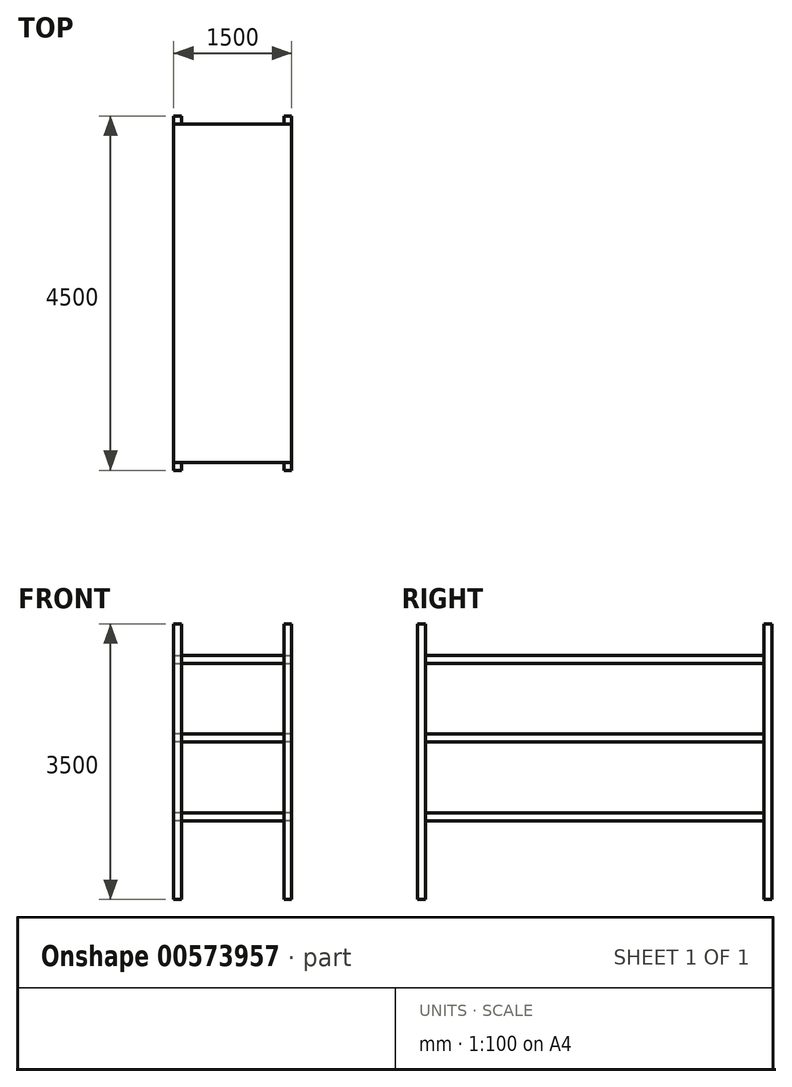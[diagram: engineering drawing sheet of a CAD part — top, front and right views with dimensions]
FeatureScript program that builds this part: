
annotation { "Feature Type Name" : "Feature", "Feature Type Description" : "" }
export const myFeature = defineFeature(function(context is Context, id is Id, definition is map)
    precondition{}
    {
        {
            var Q0;
            Q0=qCreatedBy(makeId("Top.planeOp"),FACE);
            cPlane(context, id + "F0", {"entities" : qUnion([Q0]), "cplaneType" : CPlaneType.OFFSET, "offset" : 1000 * mm, "width" : 150 * mm, "height" : 150 * mm});
        }
        {
            var Q0;
            Q0=qCreatedBy(makeId("Top.planeOp"),FACE);
            cPlane(context, id + "F1", {"entities" : qUnion([Q0]), "cplaneType" : CPlaneType.OFFSET, "offset" : 2000 * mm, "width" : 150 * mm, "height" : 150 * mm});
        }
        {
            var Q0;
            Q0=qCreatedBy(makeId("Top.planeOp"),FACE);
            cPlane(context, id + "F2", {"entities" : qUnion([Q0]), "cplaneType" : CPlaneType.OFFSET, "offset" : 3000 * mm, "width" : 150 * mm, "height" : 150 * mm});
        }
        {
            var Q0;
            Q0=qCreatedBy(makeId("Top.planeOp"),FACE);
            var sketch = newSketch(context, id + "F3", { "sketchPlane" : qUnion([Q0])});
            skPoint(sketch, "E0.middle", {"position": v(0, 0) * mm});
            skLineSegment(sketch, "E1.bottom", {"start": v(-750, 2250) * mm, "end": v(-650, 2250) * mm});
            skLineSegment(sketch, "E1.top", {"start": v(-750, 2150) * mm, "end": v(-650, 2150) * mm});
            skLineSegment(sketch, "E1.left", {"start": v(-750, 2250) * mm, "end": v(-750, 2150) * mm});
            skLineSegment(sketch, "E1.right", {"start": v(-650, 2250) * mm, "end": v(-650, 2150) * mm});
            skLineSegment(sketch, "E2.bottom", {"start": v(750, 2250) * mm, "end": v(650, 2250) * mm});
            skLineSegment(sketch, "E2.top", {"start": v(750, 2150) * mm, "end": v(650, 2150) * mm});
            skLineSegment(sketch, "E2.left", {"start": v(750, 2250) * mm, "end": v(750, 2150) * mm});
            skLineSegment(sketch, "E2.right", {"start": v(650, 2250) * mm, "end": v(650, 2150) * mm});
            skLineSegment(sketch, "E3.bottom", {"start": v(-750, -2250) * mm, "end": v(-650, -2250) * mm});
            skLineSegment(sketch, "E3.top", {"start": v(-750, -2150) * mm, "end": v(-650, -2150) * mm});
            skLineSegment(sketch, "E3.left", {"start": v(-750, -2250) * mm, "end": v(-750, -2150) * mm});
            skLineSegment(sketch, "E3.right", {"start": v(-650, -2250) * mm, "end": v(-650, -2150) * mm});
            skLineSegment(sketch, "E4.bottom", {"start": v(750, -2250) * mm, "end": v(650, -2250) * mm});
            skLineSegment(sketch, "E4.top", {"start": v(750, -2150) * mm, "end": v(650, -2150) * mm});
            skLineSegment(sketch, "E4.left", {"start": v(750, -2250) * mm, "end": v(750, -2150) * mm});
            skLineSegment(sketch, "E4.right", {"start": v(650, -2250) * mm, "end": v(650, -2150) * mm});
            skSolve(sketch);
        }
        {
            var Q0;
            Q0=qCreatedBy(id+"F0.planeOp",FACE);
            var sketch = newSketch(context, id + "F4", { "sketchPlane" : qUnion([Q0])});
            skLineSegment(sketch, "E5.bottom", {"start": v(750, -2150) * mm, "end": v(-750, -2150) * mm});
            skLineSegment(sketch, "E5.top", {"start": v(750, 2150) * mm, "end": v(-750, 2150) * mm});
            skLineSegment(sketch, "E5.left", {"start": v(750, -2150) * mm, "end": v(750, 2150) * mm});
            skLineSegment(sketch, "E5.right", {"start": v(-750, -2150) * mm, "end": v(-750, 2150) * mm});
            skPoint(sketch, "E5.middle", {"position": v(0, 0) * mm});
            skSolve(sketch);
        }
        {
            var Q0;
            Q0=qCreatedBy(id+"F1.planeOp",FACE);
            var sketch = newSketch(context, id + "F5", { "sketchPlane" : qUnion([Q0])});
            skLineSegment(sketch, "E6.bottom", {"start": v(750, 2150) * mm, "end": v(-750, 2150) * mm});
            skLineSegment(sketch, "E6.top", {"start": v(750, -2150) * mm, "end": v(-750, -2150) * mm});
            skLineSegment(sketch, "E6.left", {"start": v(750, 2150) * mm, "end": v(750, -2150) * mm});
            skLineSegment(sketch, "E6.right", {"start": v(-750, 2150) * mm, "end": v(-750, -2150) * mm});
            skPoint(sketch, "E6.middle", {"position": v(0, 0) * mm});
            skSolve(sketch);
        }
        {
            var Q0;
            Q0=qCreatedBy(id+"F2.planeOp",FACE);
            var sketch = newSketch(context, id + "F6", { "sketchPlane" : qUnion([Q0])});
            skLineSegment(sketch, "E7.bottom", {"start": v(-750, -2150) * mm, "end": v(750, -2150) * mm});
            skLineSegment(sketch, "E7.top", {"start": v(-750, 2150) * mm, "end": v(750, 2150) * mm});
            skLineSegment(sketch, "E7.left", {"start": v(-750, -2150) * mm, "end": v(-750, 2150) * mm});
            skLineSegment(sketch, "E7.right", {"start": v(750, -2150) * mm, "end": v(750, 2150) * mm});
            skPoint(sketch, "E7.middle", {"position": v(0, 0) * mm});
            skSolve(sketch);
        }
        {
            var Q0;
            Q0 = qSketchRegion(id + "F3", true);
            extrude(context, id + "F7", {"entities" : qUnion([Q0]), "depth" : 3500 * mm, "offsetDistance" : 25 * mm});
        }
        {
            var Q0;
            Q0 = qSketchRegion(id + "F4", true);
            var Q1;
            Q1 = qSketchRegion(id + "F5", true);
            extrude(context, id + "F8", {"entities" : qUnion([Q0, Q1]), "depth" : 100 * mm, "offsetDistance" : 25 * mm});
        }
        {
            var Q0;
            Q0 = qSketchRegion(id + "F6", true);
            extrude(context, id + "F9", {"entities" : qUnion([Q0]), "depth" : 100 * mm, "offsetDistance" : 25 * mm});
        }
    });
